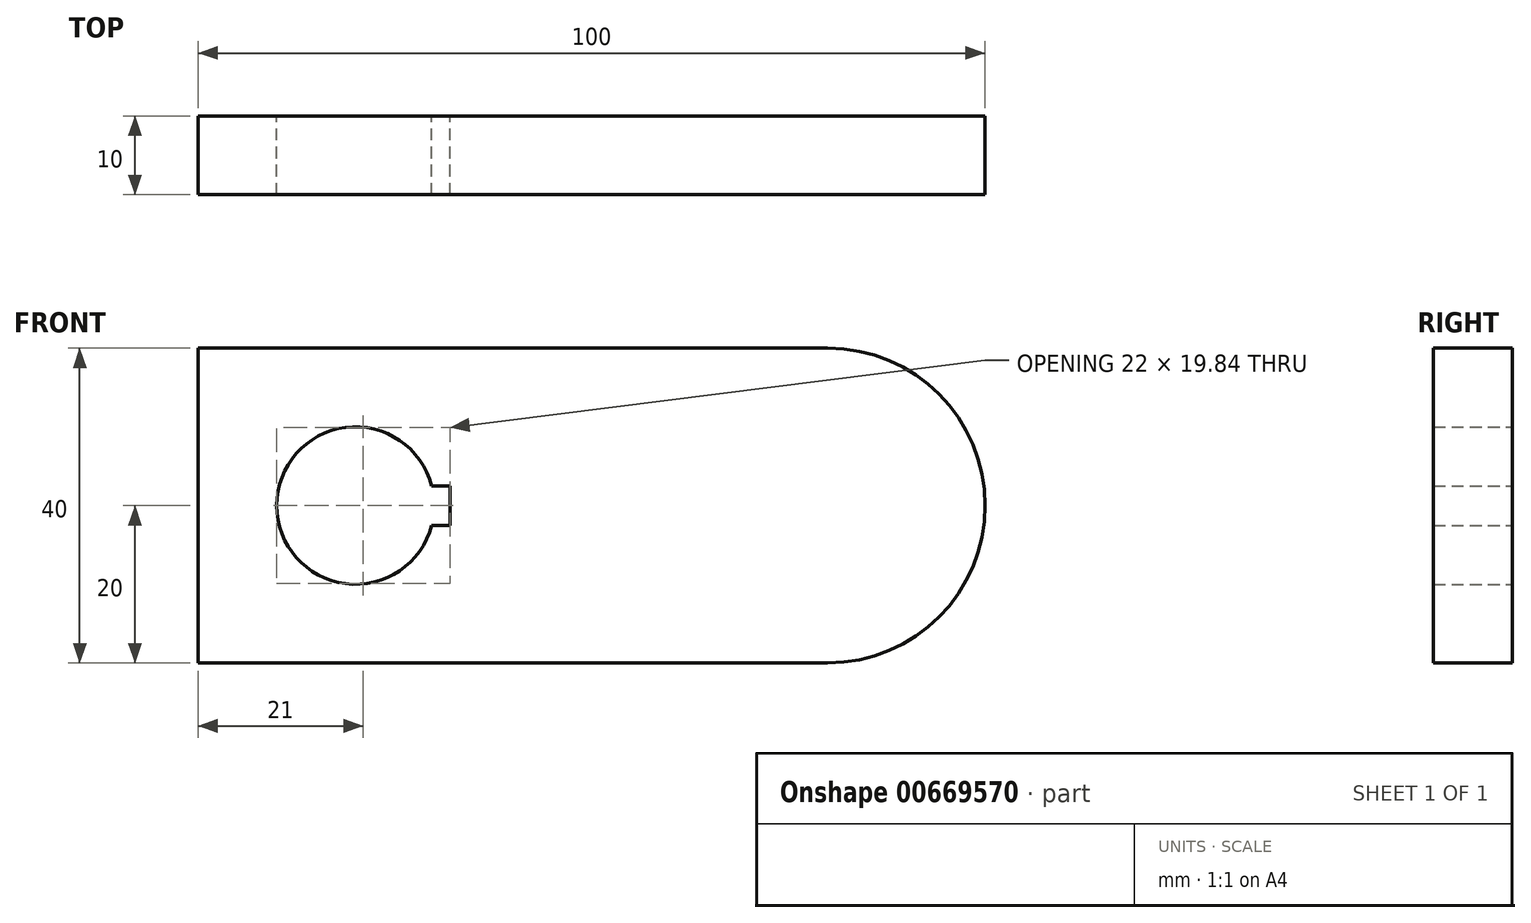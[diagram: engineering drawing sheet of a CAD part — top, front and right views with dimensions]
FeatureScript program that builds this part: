
annotation { "Feature Type Name" : "Feature", "Feature Type Description" : "" }
export const myFeature = defineFeature(function(context is Context, id is Id, definition is map)
    precondition{}
    {
        {
            var Q0;
            Q0=qCreatedBy(makeId("Front.planeOp"),FACE);
            var sketch = newSketch(context, id + "F0", { "sketchPlane" : qUnion([Q0])});
            skLineSegment(sketch, "E0", {"start": v(-20, 0) * mm, "end": v(-100, 0) * mm});
            skLineSegment(sketch, "E1", {"start": v(-100, 40) * mm, "end": v(-20, 40) * mm});
            skLineSegment(sketch, "E2", {"start": v(-100, 40) * mm, "end": v(-100, 0) * mm});
            skArc(sketch, "E3", {"start": v(-70.32, 22.5) * mm, "mid": v(-90, 20) * mm, "end": v(-70.32, 17.5) * mm});
            skArc(sketch, "E4", {"start": v(-20, 0) * mm, "mid": v(0, 20) * mm, "end": v(-20, 40) * mm});
            skLineSegment(sketch, "E5", {"start": v(-68, 20) * mm, "end": v(-68, 17.5) * mm});
            skLineSegment(sketch, "E6", {"start": v(-68, 20) * mm, "end": v(-68, 22.5) * mm});
            skLineSegment(sketch, "E7", {"start": v(-68, 22.5) * mm, "end": v(-70.32, 22.5) * mm});
            skLineSegment(sketch, "E8", {"start": v(-68, 17.5) * mm, "end": v(-70.32, 17.5) * mm});
            skSolve(sketch);
        }
        {
            var Q0;
            Q0=makeQuery(id+"F0.imprint","IMPRINT",FACE,{"disambiguationData":[TD([[makeQuery(id+"F0.imprint","IMPRINT",EDGE,{"derivedFrom":sQuery(id+"F0.wireOp",EDGE,"E0")}),-1.0]])]});
            extrude(context, id + "F1", {"entities" : qUnion([Q0]), "depth" : 10 * mm, "offsetDistance" : 25 * mm});
        }
    });
